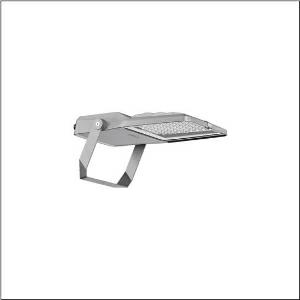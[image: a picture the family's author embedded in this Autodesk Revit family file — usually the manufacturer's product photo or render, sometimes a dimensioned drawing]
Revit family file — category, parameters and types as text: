
# Revit family: floodlight_fl_21_mini___pl52_5xa7772b3d1a_5e8e
name_source: partatom
category: Lighting Fixtures
units: mm (PartAtom-declared; Revit-internal decimal feet)

## family parameters
Cut with Voids When Loaded = No
Host = Face
Light Source = No
Part Type = Normal
Room Calculation Point = No
Round Connector Dimension = Use Diameter
Shared = No

## types (1)
- --- (1 x LED, 5370 lm, 45.5 W, 3000K)
    Apparent Load = 46 VA
    CIE Flux Codes = 26 60 98 100 100
    Color Rendering = 80
    Color Temperature = 3000K
    Default Elevation = 1800 mm
    Description = Floodlight FL 21 mini, floodlight, primary light control with lens, of PMMA, primary optical cover: protective disc, of toughened safety glass, transparent, light distribution: PL52, light emission: direct distribution, installation type: surface-mounted, LED, High Power LED, rated luminous flux: 5.370lm, luminous efficacy: 118lm/W, light colour: 830, colour temperature: 3000K, control gear: ECG iQ, control: Street-Remote, Auto-Match, Temp-Guard, Night-Set, Smart-Wire, Desk-Remote (wireless, voltage-free reading and setting of iQ features in the workshop via application-optimized NFC function/RFID function), optimised constant luminous flux control (CLO 2.0), with terminal, 6-pole, mains connection: 220..240V, AC, 50/60Hz, start of lifetime: 46W, end of lifetime: 48W, reduction: 21W, luminaire housing, of diecast aluminium, powder-coated, Siteco® metallic grey (DB 702S), corrosivity category C5 according to DIN EN ISO 12944, mounting bracket, of steel, galvanised, powder-coated, Siteco® metallic grey (DB 702S), protection rating (complete): IP66, insulation class (complete): insulation class II (safety insulation), certification: CE, ENEC, VDE, protection symbol: D, impact resistance: IK08, permissible operating ambient temperature: -40..+40°C, permissible operating ambient temperature for outdoor applications: -40..+50°C, standard: DIN EN 12944, packaging unit: 1 piece

Light Distribution: PL52
    Height = 70 mm
    Lamp = 1 x LED
    Lamp Light Flux = 5370 lm
    Lamp Power = 45.5 W
    Lamp count = 1
    Length = 485 mm
    Luminous efficacy = 118 lm/W
    Manufacturer = Siteco
    ModVariant = No
    Model = 5XA7772B3D1A
    Number of Poles = 1
    OnlyDefault = Yes
    Power Factor = 1
    Product Name = Floodlight FL 21 mini | PL52
    Product group = floodlight | pylon top
    ProductGroupID = 6101
    Protection Class = Protection class II
    Protection Degree = IP 66
    RLX_Detail_Level = 1
    RlxData = <blob elided: 96305 chars, md5=5553a1a3>
    Socket = socket
    Standby Power = 0 W
    System Light Flux = 5370 lm
    System Power = 46 W
    Type Comments = factory setting: luminous flux: 100 % | dim-lin: 254 | 463 mA
    Type Image = l_1006845.jpg
    URL = http://relux.com
    VarID = @adj_075927
    Voltage = 0 V
    Weight = 0.00 kg
    Width = 337 mm

## geometry (parser evidence)
native form markers: Blend x4, Sweep x14
no freeform markers — native parametric forms only
